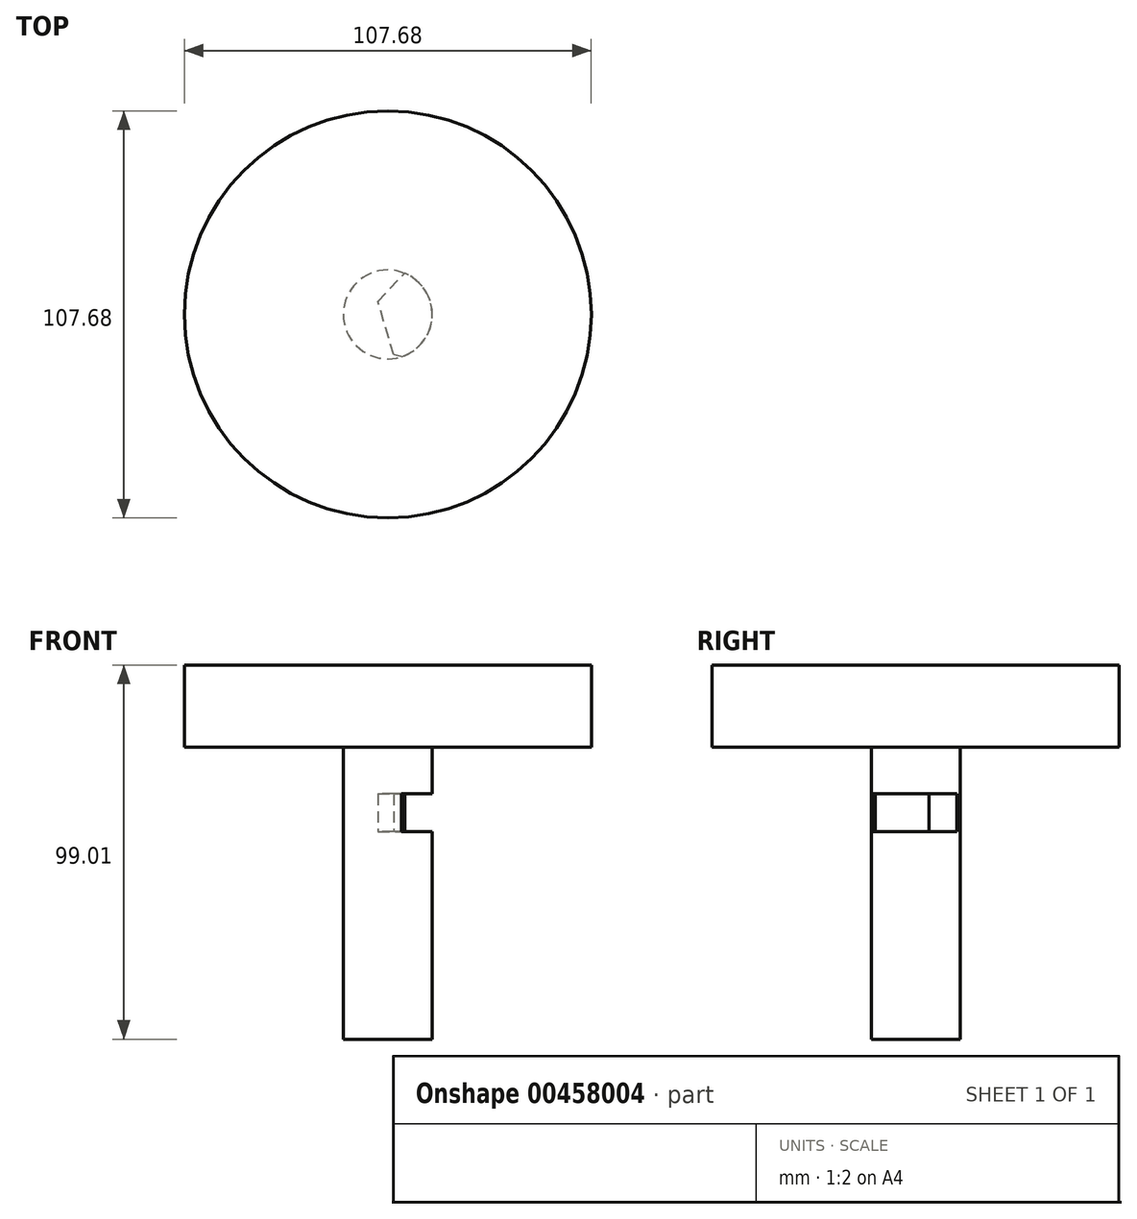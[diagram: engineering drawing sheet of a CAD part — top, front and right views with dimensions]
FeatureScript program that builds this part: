
annotation { "Feature Type Name" : "Feature", "Feature Type Description" : "" }
export const myFeature = defineFeature(function(context is Context, id is Id, definition is map)
    precondition{}
    {
        {
            var Q0;
            Q0=qCreatedBy(makeId("Front.planeOp"),FACE);
            var sketch = newSketch(context, id + "F0", { "sketchPlane" : qUnion([Q0])});
            skLineSegment(sketch, "E0", {"start": v(0, 44.1) * mm, "end": v(42.08, 44.1) * mm});
            skLineSegment(sketch, "E1", {"start": v(42.08, 44.1) * mm, "end": v(42.08, 22.43) * mm});
            skLineSegment(sketch, "E2", {"start": v(42.08, 22.43) * mm, "end": v(0, 22.43) * mm});
            skLineSegment(sketch, "E3", {"start": v(0, 22.43) * mm, "end": v(0, -54.92) * mm});
            skLineSegment(sketch, "E4", {"start": v(0, -54.92) * mm, "end": v(-11.76, -54.92) * mm});
            skLineSegment(sketch, "E5", {"start": v(-11.76, -54.92) * mm, "end": v(-11.76, 44.1) * mm});
            skLineSegment(sketch, "E6", {"start": v(-11.76, 44.1) * mm, "end": v(1.24, 44.1) * mm});
            skSolve(sketch);
        }
        {
            var Q0;
            Q0 = qSketchRegion(id + "F0", true);
            var Q1;
            Q1=sQuery(id+"F0.wireOp",EDGE,"E5");
            revolve(context, id + "F1", {"entities" : qUnion([Q0]), "axis" : qUnion([Q1]), "revolveType" : RevolveType.FULL});
        }
        {
            var Q0;
            Q0=qCreatedBy(makeId("Top.planeOp"),FACE);
            var sketch = newSketch(context, id + "F2", { "sketchPlane" : qUnion([Q0])});
            skCircle(sketch, "E7.cCircle", {"center": v(0, 0) * mm, "radius": 12.8 * mm, "construction": true});
            skLineSegment(sketch, "E7.0", {"start": v(-14.37, 3.46) * mm, "end": v(-4.2, 14.18) * mm});
            skLineSegment(sketch, "E7.1", {"start": v(-4.2, 14.18) * mm, "end": v(10.18, 10.72) * mm});
            skLineSegment(sketch, "E7.2", {"start": v(10.18, 10.72) * mm, "end": v(14.37, -3.46) * mm});
            skLineSegment(sketch, "E7.3", {"start": v(14.37, -3.46) * mm, "end": v(4.2, -14.18) * mm});
            skLineSegment(sketch, "E7.4", {"start": v(4.2, -14.18) * mm, "end": v(-10.18, -10.72) * mm});
            skLineSegment(sketch, "E7.5", {"start": v(-10.18, -10.72) * mm, "end": v(-14.37, 3.46) * mm});
            skPoint(sketch, "E7.0.midPoint", {"position": v(-9.28, 8.82) * mm});
            skSolve(sketch);
        }
        {
            var Q0;
            Q0 = qSketchRegion(id + "F2", true);
            extrude(context, id + "F3", {"entities" : qUnion([Q0]), "operationType" : NewBodyOperationType.REMOVE, "depth" : 10 * mm});
        }
    });
